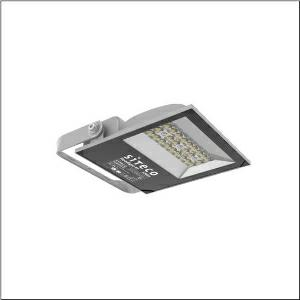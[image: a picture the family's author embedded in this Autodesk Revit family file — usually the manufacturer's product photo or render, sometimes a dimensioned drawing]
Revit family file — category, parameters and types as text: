
# Revit family: floodlight_fl_41_mini___pl32_5xa8571a1121_0023
name_source: partatom
category: Lighting Fixtures
units: mm (PartAtom-declared; Revit-internal decimal feet)

## family parameters
Cut with Voids When Loaded = No
Host = Face
Light Source = No
Part Type = Normal
Room Calculation Point = No
Round Connector Dimension = Use Diameter
Shared = No

## types (1)
- --- (1 x LED, 13000 lm, 100 W, 3000K)
    Apparent Load = 100 VA
    CIE Flux Codes = 40 79 99 100 100
    Color Rendering = 70
    Color Temperature = 3000K
    Default Elevation = 1800 mm
    Description = Floodlight FL 41 mini, floodlight, primary light control with lens, of PMMA, primary optical cover: protective disc, transparent, light distribution: PL32, light emission: direct distribution, installation type: surface-mounted, LED, High Power LED, rated luminous flux: 13.000lm, luminous efficacy: 130lm/W, light colour: 730, colour temperature: 3000K, control gear: ON/OFF Multilumen, with cable, 3x 1.5mm², mains connection: 220..240V, AC, 50/60Hz, connection cable pre-assembled, cable length: 2m, rated input power: 100W, luminaire housing, of diecast aluminium, powder-coated, metallic grey (RAL 9006), length: 265mm, width: 245mm, height: 54mm, protection rating (complete): IP65, insulation class (complete): insulation class I (protective earthing), certification: CE, ENEC, impact resistance: IK08, permissible operating ambient temperature: -40..+40°C, permissible storage temperature: -40..+60°C, packaging unit: 1 piece

Light Distribution: PL32
    Height = 54 mm
    Lamp = 1 x LED
    Lamp Light Flux = 13000 lm
    Lamp Power = 100 W
    Lamp count = 1
    Length = 226 mm
    Luminous efficacy = 130 lm/W
    Manufacturer = Siteco
    ModVariant = No
    Model = 5XA8571A1121
    Mounting Place = Ceiling
    Mounting Type = Surface mounted
    Number of Poles = 1
    OnlyDefault = Yes
    Power Factor = 1
    Product Name = Floodlight FL 41 mini | PL32
    Product group = floodlight | ceiling mounted
    ProductGroupID = 301
    Protection Class = Protection class I
    Protection Degree = IP 65
    RLX_Detail_Level = 1
    RLX_Emergency_Light_Flux = 0 lm
    RLX_Emergency_Type = 0
    RLX_Emergency_Type_DB = No
    RlxData = <blob elided: 24629 chars, md5=dd33a5f3>
    Socket = socket
    Standby Power = 0 W
    System Light Flux = 13000 lm
    System Power = 100 W
    Type Comments = factory setting: luminous flux: 100 % | (OFF | OFF | OFF)
    Type Image = l_1248226.jpg
    URL = http://relux.com
    VarID = @adj_131680
    Voltage = 0 V
    Weight = 0.00 kg
    Width = 241 mm

## geometry (parser evidence)
native form markers: Blend x4, Sweep x11
no freeform markers — native parametric forms only
